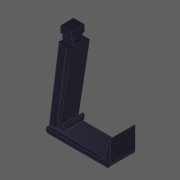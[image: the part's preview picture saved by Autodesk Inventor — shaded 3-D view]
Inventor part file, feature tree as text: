
AUTODESK INVENTOR PART (.ipt)
format: ipt  version: 2020 (Build 240168000, 168)  size: 281,088 bytes
history: native  units: in
note: dims shown in document units (in); Inventor stores cm internally (conversion verified against a paired STEP export)
features: fillet x5, other x3, extrude x3
ambient origin geometry x8: Origin, YZ Plane, XZ Plane, XY Plane, X Axis, Y Axis, Z Axis, Center Point
bodies: Solid1 (feature_tree)
feature tree (11):
  other  "Neck Start Plane"
  other  "Arm Profile"
  extrude  "Main Arm"  Depth=0.0039in
  extrude  "Pincher"  Depth=1.0386in
  extrude  "Neck"  Depth=0.7283in
  fillet  "Spring Hook Fillet"  Radius=0.1181in
  fillet  "Spring Attachment Fillet"  [1 undecoded]
  fillet  "Soft Edges"  Radius=0.195in
  fillet  "Pincher Fillet 1"  Radius=0.0197in
  fillet  "Pincher Fillet 2"  Radius=0.0394in
  other  "Neck Sketch"
note: 1 required parameter value undecoded (feature->parameter linkage not recoverable at this tier; creation-order binding heuristic only, values carry confidence <= 0.55)
